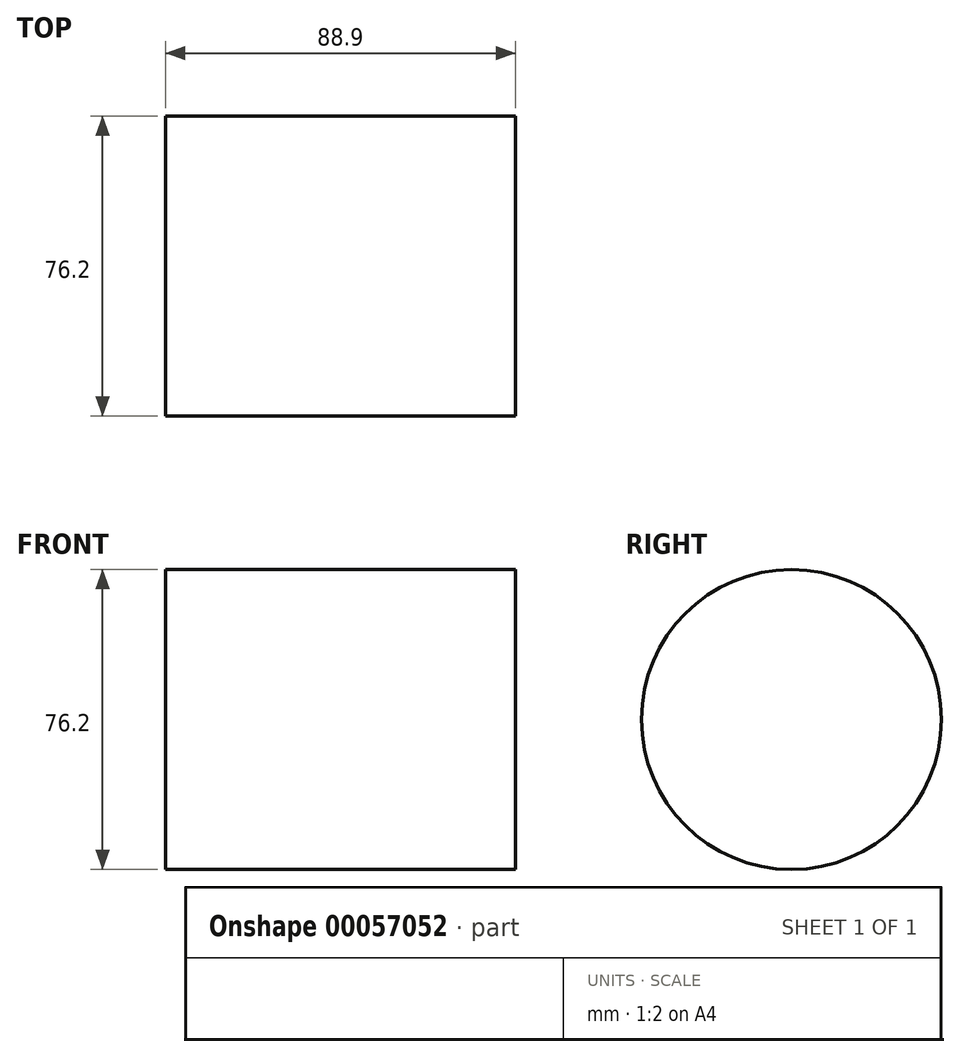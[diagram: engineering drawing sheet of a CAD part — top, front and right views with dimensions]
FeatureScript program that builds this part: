
annotation { "Feature Type Name" : "Feature", "Feature Type Description" : "" }
export const myFeature = defineFeature(function(context is Context, id is Id, definition is map)
    precondition{}
    {
        {
            var Q0;
            Q0=qCreatedBy(makeId("Right.planeOp"),FACE);
            var sketch = newSketch(context, id + "F0", { "sketchPlane" : qUnion([Q0])});
            skCircle(sketch, "E0", {"center": v(0, 0) * mm, "radius": 38.1 * mm});
            skSolve(sketch);
        }
        {
            var Q0;
            Q0 = qSketchRegion(id + "F0", true);
            extrude(context, id + "F1", {"entities" : qUnion([Q0]), "oppositeDirection" : true, "depth" : 88.9 * mm});
        }
    });
